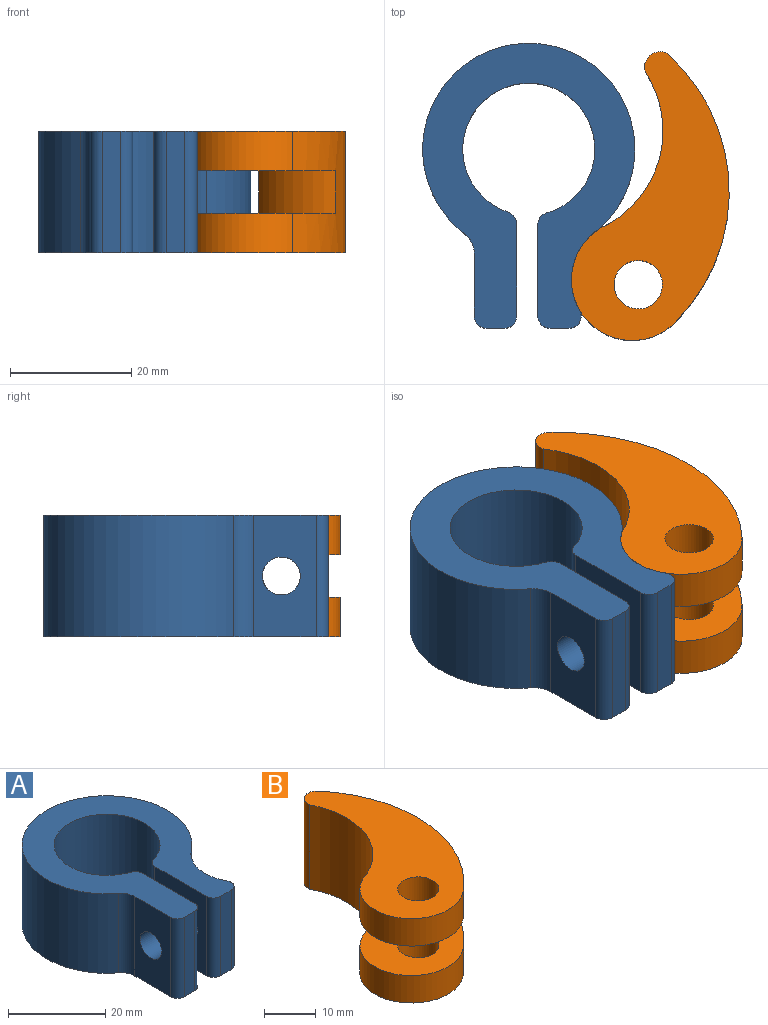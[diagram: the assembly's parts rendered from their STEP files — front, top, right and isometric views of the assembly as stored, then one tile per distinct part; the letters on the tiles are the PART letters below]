
ASSEMBLY  parts=2 mates=1
PART A: 19 faces, bbox 35x47x20 mm
  f0: cylinder r=10mm len=20mm, axis (0,0,-1), area 235.5mm2, adj f1,f14,f15,f16,f17
  f1: cylinder r=17.5mm len=35mm, axis (0,0,-1), area 1755.7mm2, adj f0,f2,f15,f16
  f2: cylinder r=4mm len=20mm, axis (0,0,-1), area 73.7mm2, adj f1,f3,f15,f16
  f3: plane 20x10.38mm, normal (-1,0,0), area 176.9mm2, adj f2,f4,f15,f16,f18
  f4: cylinder r=2mm len=20mm, axis (0,0,-1), area 62.8mm2, adj f3,f5,f15,f16
  f5: plane 20x3mm, normal (0,-1,0), area 60mm2, adj f4,f6,f15,f16
  f6: cylinder r=2mm len=20mm, axis (0,0,-1), area 62.8mm2, adj f5,f7,f15,f16
  f7: plane 20x15.24mm, normal (1,0,0), area 274.1mm2, adj f6,f8,f15,f16,f18
  f8: cylinder r=2mm len=20mm, axis (0,0,-1), area 50.2mm2, adj f7,f9,f15,f16
  f9: cylinder r=10.9mm len=21.8mm, axis (0,0,-1), area 1241.1mm2, adj f8,f10,f15,f16
  f10: cylinder r=2mm len=20mm, axis (0,0,-1), area 51.8mm2, adj f9,f11,f15,f16
  f11: plane 20x15.08mm, normal (-1,0,0), area 271mm2, adj f10,f12,f15,f16,f17
  f12: cylinder r=2mm len=20mm, axis (0,0,-1), area 62.8mm2, adj f11,f13,f15,f16
  f13: plane 20x3.12mm, normal (0,-1,0), area 62.4mm2, adj f12,f14,f15,f16
  f14: cylinder r=2mm len=20mm, axis (0,0,-1), area 83.7mm2, adj f0,f13,f15,f16
  f15: plane 47x35mm, normal (0,0,1), area 733.6mm2, adj f0,f1,f2,f3,f4,f5,f6,f7
  f16: plane 47x35mm, normal (0,0,-1), area 733.6mm2, adj f0,f1,f2,f3,f4,f5,f6,f7
  f17: cylinder r=3.12mm len=6.25mm, axis (-1,0,0), area 113.3mm2, adj f0,f11
  f18: cylinder r=3.12mm len=7mm, axis (-1,0,0), area 137.4mm2, adj f3,f7
PART B: 12 faces, bbox 27.7x46.9x20 mm
  f0: cylinder r=17.61mm len=24.87mm, axis (0,0,-1), area 548.2mm2, adj f1,f4,f5,f6,f7,f9,f10,f11
  f1: cylinder r=10mm len=19.01mm, axis (0,0,-1), area 221.3mm2, adj f0,f2,f7,f10
  f2: cylinder r=30.54mm len=43.95mm, axis (0,0,-1), area 890.2mm2, adj f1,f4,f5,f6,f7,f9,f10,f11
  f3: cylinder r=4mm len=8mm, axis (0,0,1), area 163.4mm2, adj f7,f10
  f4: cylinder r=10mm len=19.01mm, axis (0,0,-1), area 221.3mm2, adj f0,f2,f6,f11
  f5: cylinder r=2.59mm len=20mm, axis (0,0,-1), area 120.7mm2, adj f0,f2,f6,f7
  f6: plane 46.85x27.75mm, normal (0,0,1), area 612.8mm2, adj f0,f2,f4,f5,f8
  f7: plane 46.85x27.75mm, normal (0,0,-1), area 612.8mm2, adj f0,f1,f2,f3,f5
  f8: cylinder r=4mm len=8mm, axis (0,0,1), area 163.4mm2, adj f6,f11
  f9: cylinder r=14.92mm len=11.45mm, axis (0,0,1), area 116.8mm2, adj f0,f2,f10,f11
  f10: plane 24.82x23.96mm, normal (0,0,1), area 308.3mm2, adj f0,f1,f2,f3,f9
  f11: plane 24.82x23.96mm, normal (0,0,-1), area 308.3mm2, adj f0,f2,f4,f8,f9
PLACE A t=(-8.26,5.38,-3.77)mm fixed
PLACE B rot(axis=(0,0,1),6.4deg) t=(8.76,-16.13,-3.77)mm
MATE revolute A.f0 <-> B.f1  axis (0,0,1) through (8.76,-16.13,16.23)mm
